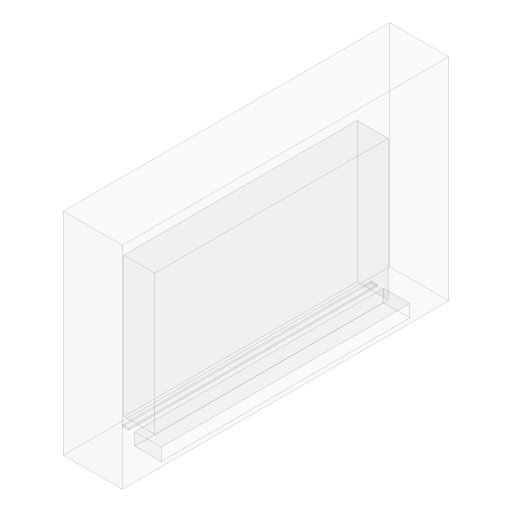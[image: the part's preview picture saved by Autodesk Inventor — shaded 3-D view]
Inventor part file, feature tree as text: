
AUTODESK INVENTOR PART (.ipt)
format: ipt  version: 2023 (Build 270158000, 158)  size: 284,160 bytes
history: native  units: mm
features: sketch x20, extrude x17, projected_geometry x10, plane x8, fillet x4
ambient origin geometry x8: Origin, YZ Plane, XZ Plane, XY Plane, X Axis, Y Axis, Z Axis, Center Point
bodies: 实体1 (feature_tree)
feature tree (59):
  extrude  "拉伸1"  Depth=1050.0mm
  fillet  "圆角1"  Radius=190.0mm
  extrude  "拉伸2"  Depth=100.0mm
  extrude  "拉伸3"  Depth=50.0mm
  extrude  "拉伸4"  Depth=100.0mm TaperAngle=0.0deg
  extrude  "拉伸5"  Depth=80.0mm
  plane  "工作平面1"
  extrude  "拉伸6"  Depth=800.0mm
  fillet  "圆角3"  Radius=40.0mm
  plane  "工作平面2"
  sketch  "草图7"  dims[d19=75.0mm d20=105.0mm d21=0.0mm]
  extrude  "拉伸7"  Depth=105.0mm TaperAngle=0.0deg
  extrude  "拉伸8"  Depth=100.0mm
  plane  "工作平面3"
  extrude  "拉伸9"  Depth=150.0mm
  fillet  "圆角4"  Radius=45.0mm
  plane  "工作平面4"
  plane  "工作平面5"
  plane  "工作平面6"
  sketch  "草图11"  dims[d31=-300.0mm d32=500.0mm d33=0.0mm]
  plane  "工作平面7"
  sketch  "草图12"  dims[d34=55.0mm d35=40.0mm]
  extrude  "拉伸10"  Depth=5.0mm
  extrude  "拉伸11"  Depth=500.0mm TaperAngle=0.0deg
  extrude  "拉伸12"  Depth=40.0mm
  extrude  "拉伸13"  Depth=500.0mm TaperAngle=0.0deg
  fillet  "圆角5"  [1 undecoded]
  extrude  "拉伸14"  Depth=60.0mm
  plane  "工作平面8"
  extrude  "拉伸15"  Depth=20.0mm
  extrude  "拉伸16"  Depth=5.0mm
  extrude  "拉伸17"  [1 undecoded]
  sketch  "草图1"  dims[d0=680.0mm d1=1050.0mm d2=190.0mm d3=0.0mm]
  sketch  "草图2"  dims[d4=50.0mm d5=100.0mm]
  projected_geometry  "投影回路1"
  sketch  "草图3"  dims[d6=50.0mm d7=0.0mm d8=850.0mm]
  sketch  "草图4"  dims[d9=100.0mm d10=100.0mm d11=0.0mm]
  sketch  "草图5"  dims[d12=80.0mm d13=850.0mm]
  projected_geometry  "投影回路2"
  sketch  "草图6"  dims[d14=600.0mm d15=0.0mm d16=800.0mm d17=40.0mm]
  projected_geometry  "投影回路3"
  projected_geometry  "投影回路4"
  sketch  "草图8"  dims[d22=-175.0mm d23=100.0mm]
  sketch  "草图9"  dims[d24=750.0mm d25=150.0mm d26=45.0mm]
  sketch  "草图10"  dims[d27=450.0mm d28=0.0mm d30=5.0mm]
  projected_geometry  "投影回路5"
  projected_geometry  "投影回路6"
  projected_geometry  "投影回路7"
  projected_geometry  "投影回路8"
  sketch  "草图13"  dims[d36=30.0mm d37=500.0mm d38=0.0mm d39=-65.0mm]
  sketch  "草图14"  dims[d40=800.0mm d41=60.0mm]
  projected_geometry  "投影回路9"
  projected_geometry  "投影回路10"
  sketch  "草图15"  dims[d42=60.0mm d43=0.0mm d44=20.0mm]
  sketch  "草图16"  dims[d45=5.0mm d46=10.0mm]
  sketch  "草图17"  dims[d47=50.0mm d48=-300.0mm]
  sketch  "草图18"  dims[d49=20.0mm]
  sketch  "草图19"  dims[d50=40.0mm]
  sketch  "草图20"  dims[d51=20.0mm d52=900.0mm d53=0.0mm d54=20.0mm d55=40.0mm d56=20.0mm d57=20.0mm d58=800.0mm d59=0.0mm d60=45.0mm d61=5.0mm d62=800.0mm d63=0.0mm d64=5.0mm d65=0.0mm d66=3.0mm d67=20.0mm d68=5.0mm d69=20.0mm d70=5.0mm d71=20.0mm d72=800.0mm d73=0.0mm d74=-300.0mm d75=800.0mm d76=0.0mm d77=20.0mm d78=0.0mm d79=800.0mm d80=0.0mm]
note: 2 required parameter values undecoded (feature->parameter linkage not recoverable at this tier; creation-order binding heuristic only, values carry confidence <= 0.55)
